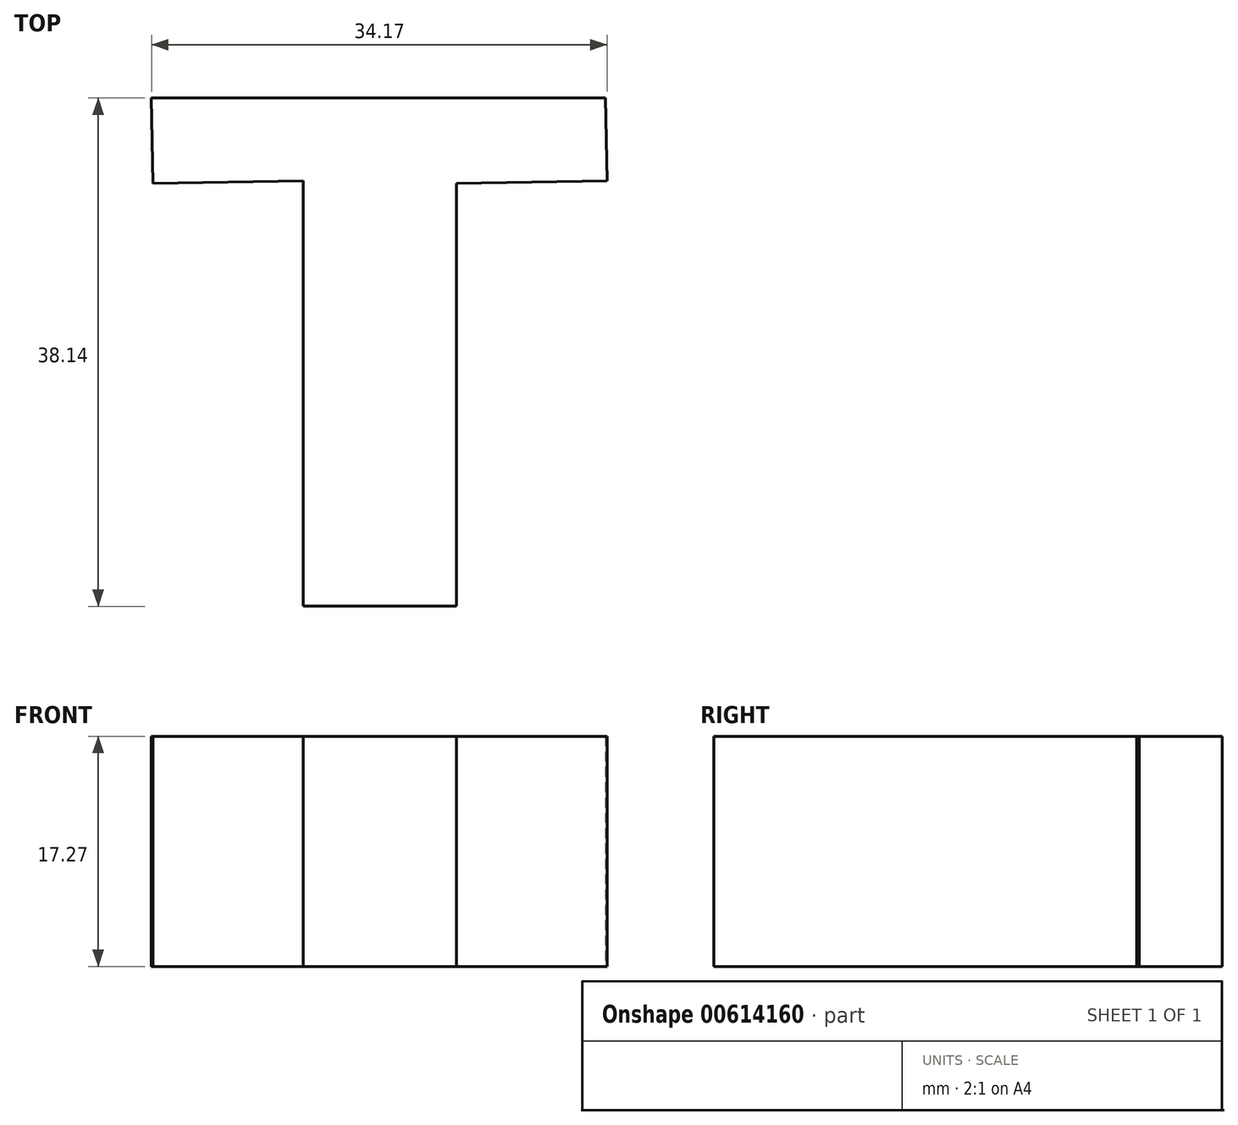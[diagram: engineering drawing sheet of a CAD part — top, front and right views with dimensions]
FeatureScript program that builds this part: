
annotation { "Feature Type Name" : "Feature", "Feature Type Description" : "" }
export const myFeature = defineFeature(function(context is Context, id is Id, definition is map)
    precondition{}
    {
        {
            var Q0;
            Q0=qCreatedBy(makeId("Top.planeOp"),FACE);
            var sketch = newSketch(context, id + "F0", { "sketchPlane" : qUnion([Q0])});
            skLineSegment(sketch, "E0", {"start": v(0, -18.79) * mm, "end": v(-5.74, -18.79) * mm});
            skLineSegment(sketch, "E1", {"start": v(-5.74, -18.79) * mm, "end": v(-5.74, 13.14) * mm});
            skLineSegment(sketch, "E2", {"start": v(0, -18.79) * mm, "end": v(5.74, -18.79) * mm});
            skLineSegment(sketch, "E3", {"start": v(5.74, -18.79) * mm, "end": v(5.74, 12.95) * mm});
            skLineSegment(sketch, "E4", {"start": v(-5.74, 13.14) * mm, "end": v(-17.03, 12.95) * mm});
            skLineSegment(sketch, "E5", {"start": v(-17.03, 12.95) * mm, "end": v(-17.14, 19.35) * mm});
            skLineSegment(sketch, "E6", {"start": v(-17.14, 19.35) * mm, "end": v(14.7, 19.35) * mm});
            skLineSegment(sketch, "E7", {"start": v(5.74, 12.95) * mm, "end": v(17.03, 13.14) * mm});
            skLineSegment(sketch, "E8", {"start": v(17.03, 13.14) * mm, "end": v(16.93, 19.35) * mm});
            skLineSegment(sketch, "E9", {"start": v(16.93, 19.35) * mm, "end": v(14.7, 19.35) * mm});
            skSolve(sketch);
        }
        {
            var Q0;
            Q0=makeQuery(id+"F0.imprint","IMPRINT",FACE,{"disambiguationData":[TD([[makeQuery(id+"F0.imprint","IMPRINT",EDGE,{"derivedFrom":sQuery(id+"F0.wireOp",EDGE,"E0")}),-1.0]])]});
            extrude(context, id + "F1", {"entities" : qUnion([Q0]), "depth" : 17.27 * mm, "offsetDistance" : 25.4 * mm});
        }
    });
